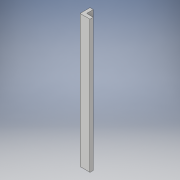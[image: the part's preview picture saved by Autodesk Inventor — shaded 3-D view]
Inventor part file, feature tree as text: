
AUTODESK INVENTOR PART (.ipt)
format: ipt  version: 2017 (Build 210142000, 142)  size: 115,200 bytes
history: native  units: in
note: dims shown in document units (in); Inventor stores cm internally (conversion verified against a paired STEP export)
features: extrude x3, sketch x3
ambient origin geometry x8: Origin, YZ Plane, XZ Plane, XY Plane, X Axis, Y Axis, Z Axis, Center Point
bodies: Solid1 (feature_tree)
feature tree (6):
  extrude  "Extrusion1"  Depth=1.0in
  extrude  "Extrusion2"  Depth=2.0in TaperAngle=0.0deg
  extrude  "Extrusion4"  Depth=40.0in
  sketch  "Sketch1"  dims[d0=1.0in d1=1.0in]
  sketch  "Sketch2"  dims[d2=40.0in d3=0.0in d4=2.0in d5=0.0in]
  sketch  "Sketch4"  dims[d8=1.0in d9=40.0in d10=2.0in d11=0.0in]
